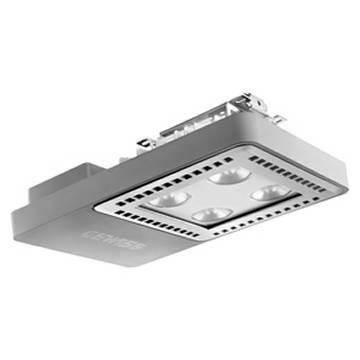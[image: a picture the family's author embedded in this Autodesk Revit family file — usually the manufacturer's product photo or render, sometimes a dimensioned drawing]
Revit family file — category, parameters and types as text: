
# Revit family: Lighting-Industriale-GEWISS-SMART[4]HE_APPARECCHI-LED_EMERGENZA_1M
name_source: partatom
category: Apparecchi per illuminazione
units: mm (PartAtom-declared; Revit-internal decimal feet)

## family parameters
Basato su piano di lavoro = Sì
Condiviso = No
Numero OmniClass = 23.80.70.00
Punto di calcolo locali = No
Quota connettore circolare = Usa diametro
Sempre verticale = No
Sorgente d'illuminazione = No
Taglio con vuoti quando caricato = No
Tipo di parte = Normale
Titolo OmniClass = Lighting

## types (1)
- Lighting-Industriale-GEWISS-SMART[4]HE_APPARECCHI-LED_EMERGENZA_1M
    Alimentatore = Incluso
    Apparecchio a ridotta temperatura superficiale = Si
    Applicazione = Interno
    Batteria = <Per categoria>
    Cablaggio = Con connettore stagno Gw connect
    Caratteristiche elettriche e gestione della luce = -
    Caratteristiche ottiche e illuminotecniche = -
    Carico apparente = 53 VA
    Catalogo = LIGHTING
    Certificazione DIN 18032-3 = -
    Certificazioni e classificazioni = -
    Classe fotobiologica = RG0
    Classe isolamento = I
    Classificazione = Lighting
    Classificazione: = -
    Codice Electrocod = 2444
    Codice digitale univoco (Datamatrix) = Datamatrix
    Colore = Grigio RAL 7035
    Contesto = Illuminazione di logistiche e locali produttivi industriali
    Controllo abbagliamento e luminanza = -
    Corpo = PA6 “Halogen Free” caricato fibra vetro
    Descrizione = SMART[4]LB 1M EMERG ELL.57K
    Dispositivo di protezione = DM 6 kV / CM 10 kV
    Distanza tot_plafoniera = 74 mm  [stored 0.242782 ft]
    Durata di vita = L90B10 (Tq+25°C) = 100.000 h - L90B10 (Tq+50°C) = 50.000 h
    Efficienza luminosa (lm/W) = 119
    Finitura colore = Grigio RAL 7035
    Fissaggio = -
    Flusso luminoso apparecchio (lm) = 6300 (750 Emerg.)
    Fotometrico = GWL1093E-CL11813-16I - EME.IES
    Frequenza nominale (Hz) = 50/60 Hz
    Gancio di chiusura = -
    Garanzia = 5 anni
    Grado di protezione = IP65
    Gruppo ottico = Riflettore in PC metallizzato e lenti in PMMA
    Guarnizioni = tipo siliconico antinvecchiamento
    IDF = 76bf5428-5d64-4f01-bcc4-d24df6228e89
    IDT = 99cc2ba6225c472dbcbc7a8f8b209142
    IPEA = -
    Immagine tipo = GWL1093E.jpg
    Inclinazione = -
    Indice di resa cromatica = CRI-80
    Informazioni generali = -
    Installazione e manutenzione = -
    Lampada = LED
    Larghezza = 253 mm  [stored 0.830052 ft]
    Lunghezza = 383 mm  [stored 1.25656 ft]
    Materiali = -
    Modello = GWS4124AQ857
    Norma di riferimento = EN 60598-2-22 ; EN 60598-1 ; EN 60598-2-24
    Ottica = Ellittica
    Peso (kg): = 5
    Plafoniera = <Per categoria>
    Potenza assorbita : = 48 W (+5W Emerg.)
    Produttore = GEWISS S.p.A.
    Prospetto di default = 1219 mm
    Raggio led = 30 mm  [stored 0.0984252 ft]
    Resistenza agli urti = IK08
    Resistenza al filo incandescente = 850 °C
    Scheda Tecnica = https://www.gewiss.com
    Schermo = Vetro Temprato Spessore 4mm
    Sistema di controllo = 1 x DALI DT6 + 1 x DALI DT1 (Emerg. 3h)
    Sostituibilità gruppo ottico = Non sostituibile
    Sostituibilità piastra di cablaggio = Solo batteria NiMh
    Spessore plafoniera = 40 mm  [stored 0.131234 ft]
    Superficie massima esposta al vento : = 0,140 m²
    Temperatura di colore = 5700K
    Temperatura di esercizio = 0 ÷ +40 °C
    Temperatura di stoccaggio = -40 +70 °C
    Tensione di alimentazione = 220 - 240 V
    Tipo di apparecchio = Riflettore industriale a LED&nbsp;
    Tipo di installazione e montaggio = Plafone - Sospensione
    Tipologia sorgente luminosa = LED - Non sostituibile
    Tolleranza cromatica = SDCM = 3
    Trasformatore = <Per categoria>
    URL = https://www.gewiss.com
    Vano di alimentazione = Integrato
    Versione file RFA = 20.11
    Vetro acceso = Lampada accesa
    Viti esterne = Acciaio inox
    Voltaggio = 230 V

note: [stored X ft] marks values corroborated as IEEE doubles in the binary element streams (Revit-internal decimal feet)

## geometry (parser evidence)
native form markers: Blend x4
no freeform markers — native parametric forms only
